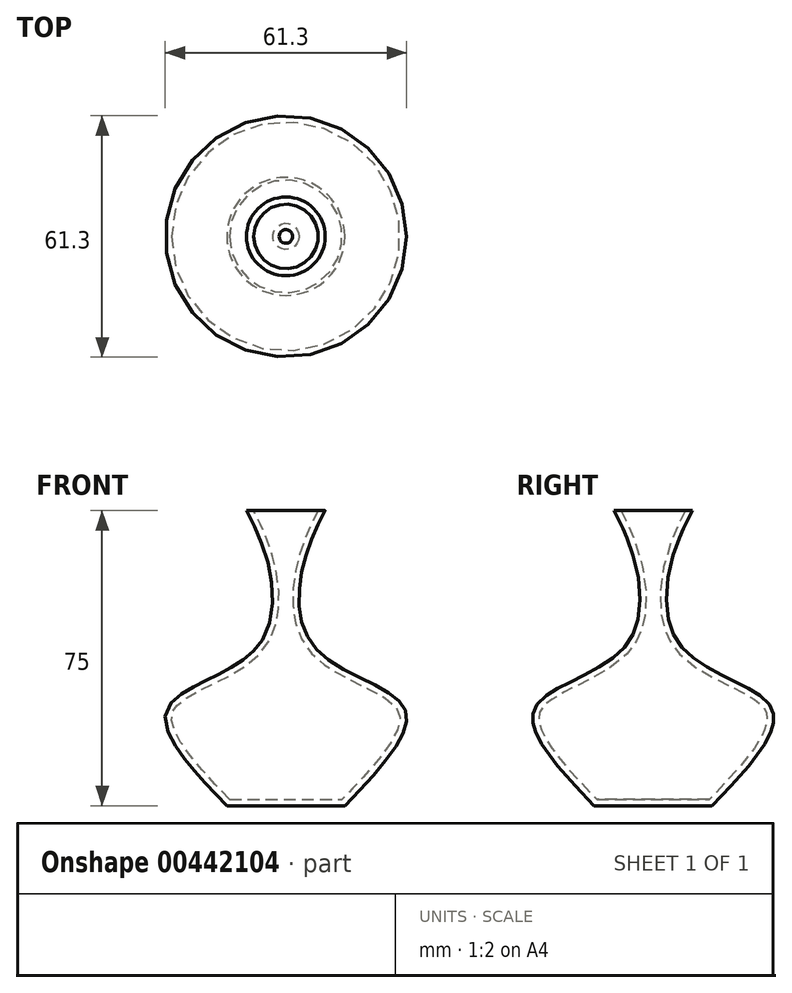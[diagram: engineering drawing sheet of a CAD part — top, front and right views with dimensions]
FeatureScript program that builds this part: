
annotation { "Feature Type Name" : "Feature", "Feature Type Description" : "" }
export const myFeature = defineFeature(function(context is Context, id is Id, definition is map)
    precondition{}
    {
        {
            var Q0;
            Q0=qCreatedBy(makeId("Top.planeOp"),FACE);
            var sketch = newSketch(context, id + "F0", { "sketchPlane" : qUnion([Q0])});
            skCircle(sketch, "E0", {"center": v(0, 0) * mm, "radius": 15 * mm});
            skSolve(sketch);
        }
        {
            var Q0;
            Q0=qCreatedBy(makeId("Top.planeOp"),FACE);
            cPlane(context, id + "F1", {"entities" : qUnion([Q0]), "cplaneType" : CPlaneType.OFFSET, "offset" : 25 * mm, "width" : 150 * mm, "height" : 150 * mm});
        }
        {
            var Q0;
            Q0=qCreatedBy(makeId("Top.planeOp"),FACE);
            cPlane(context, id + "F2", {"entities" : qUnion([Q0]), "cplaneType" : CPlaneType.OFFSET, "offset" : 70 * mm, "width" : 150 * mm, "height" : 150 * mm});
        }
        {
            var Q0;
            Q0=qCreatedBy(makeId("Top.planeOp"),FACE);
            cPlane(context, id + "F3", {"entities" : qUnion([Q0]), "cplaneType" : CPlaneType.OFFSET, "offset" : 75 * mm, "width" : 150 * mm, "height" : 150 * mm});
        }
        {
            var Q0;
            Q0=qCreatedBy(id+"F1.planeOp",FACE);
            var sketch = newSketch(context, id + "F4", { "sketchPlane" : qUnion([Q0])});
            skCircle(sketch, "E1", {"center": v(0, 0) * mm, "radius": 30 * mm});
            skSolve(sketch);
        }
        {
            var Q0;
            Q0=qCreatedBy(makeId("Top.planeOp"),FACE);
            cPlane(context, id + "F5", {"entities" : qUnion([Q0]), "cplaneType" : CPlaneType.OFFSET, "offset" : 40 * mm, "width" : 150 * mm, "height" : 150 * mm});
        }
        {
            var Q0;
            Q0=qCreatedBy(id+"F5.planeOp",FACE);
            var sketch = newSketch(context, id + "F6", { "sketchPlane" : qUnion([Q0])});
            skCircle(sketch, "E2", {"center": v(0, 0) * mm, "radius": 7.5 * mm});
            skSolve(sketch);
        }
        {
            var Q0;
            Q0=qCreatedBy(id+"F2.planeOp",FACE);
            var sketch = newSketch(context, id + "F7", { "sketchPlane" : qUnion([Q0])});
            skCircle(sketch, "E3", {"center": v(0, 0) * mm, "radius": 7.5 * mm});
            skSolve(sketch);
        }
        {
            var Q0;
            Q0=qCreatedBy(id+"F3.planeOp",FACE);
            var sketch = newSketch(context, id + "F8", { "sketchPlane" : qUnion([Q0])});
            skCircle(sketch, "E4", {"center": v(0, 0) * mm, "radius": 10 * mm});
            skSolve(sketch);
        }
        {
            var Q0;
            Q0=makeQuery(id+"F0.imprint","IMPRINT",FACE,{"disambiguationData":[TD([[makeQuery(id+"F0.imprint","IMPRINT",EDGE,{"derivedFrom":sQuery(id+"F0.wireOp",EDGE,"E0")}),1.0]])]});
            var Q1;
            Q1=makeQuery(id+"F4.imprint","IMPRINT",FACE,{"disambiguationData":[TD([[makeQuery(id+"F4.imprint","IMPRINT",EDGE,{"derivedFrom":sQuery(id+"F4.wireOp",EDGE,"E1")}),1.0]])]});
            var Q2;
            Q2=makeQuery(id+"F6.imprint","IMPRINT",FACE,{"disambiguationData":[TD([[makeQuery(id+"F6.imprint","IMPRINT",EDGE,{"derivedFrom":sQuery(id+"F6.wireOp",EDGE,"E2")}),1.0]])]});
            var Q3;
            Q3=makeQuery(id+"F7.imprint","IMPRINT",FACE,{"disambiguationData":[TD([[makeQuery(id+"F7.imprint","IMPRINT",EDGE,{"derivedFrom":sQuery(id+"F7.wireOp",EDGE,"E3")}),1.0]])]});
            var Q4;
            Q4=makeQuery(id+"F8.imprint","IMPRINT",FACE,{"disambiguationData":[TD([[makeQuery(id+"F8.imprint","IMPRINT",EDGE,{"derivedFrom":sQuery(id+"F8.wireOp",EDGE,"E4")}),1.0]])]});
            loft(context, id + "F9", {"sheetProfilesArray" : [{ "sheetProfileEntities" : qUnion([Q0]) }, { "sheetProfileEntities" : qUnion([Q1]) }, { "sheetProfileEntities" : qUnion([Q2]) }, { "sheetProfileEntities" : qUnion([Q3]) }, { "sheetProfileEntities" : qUnion([Q4]) }]});
        }
        {
            var Q0;
            Q0=makeQuery(id+"F9.opLoft","CAP_FACE",FACE,{"disambiguationData":[OSD([makeQuery(id+"F8.imprint","IMPRINT",FACE,{"disambiguationData":[TD([[makeQuery(id+"F8.imprint","IMPRINT",EDGE,{"derivedFrom":sQuery(id+"F8.wireOp",EDGE,"E4")}),1.0]])]})])],"isStart":true});
            shell(context, id + "F10", {"entities" : qUnion([Q0]), "thickness" : 1.6 * mm});
        }
    });
